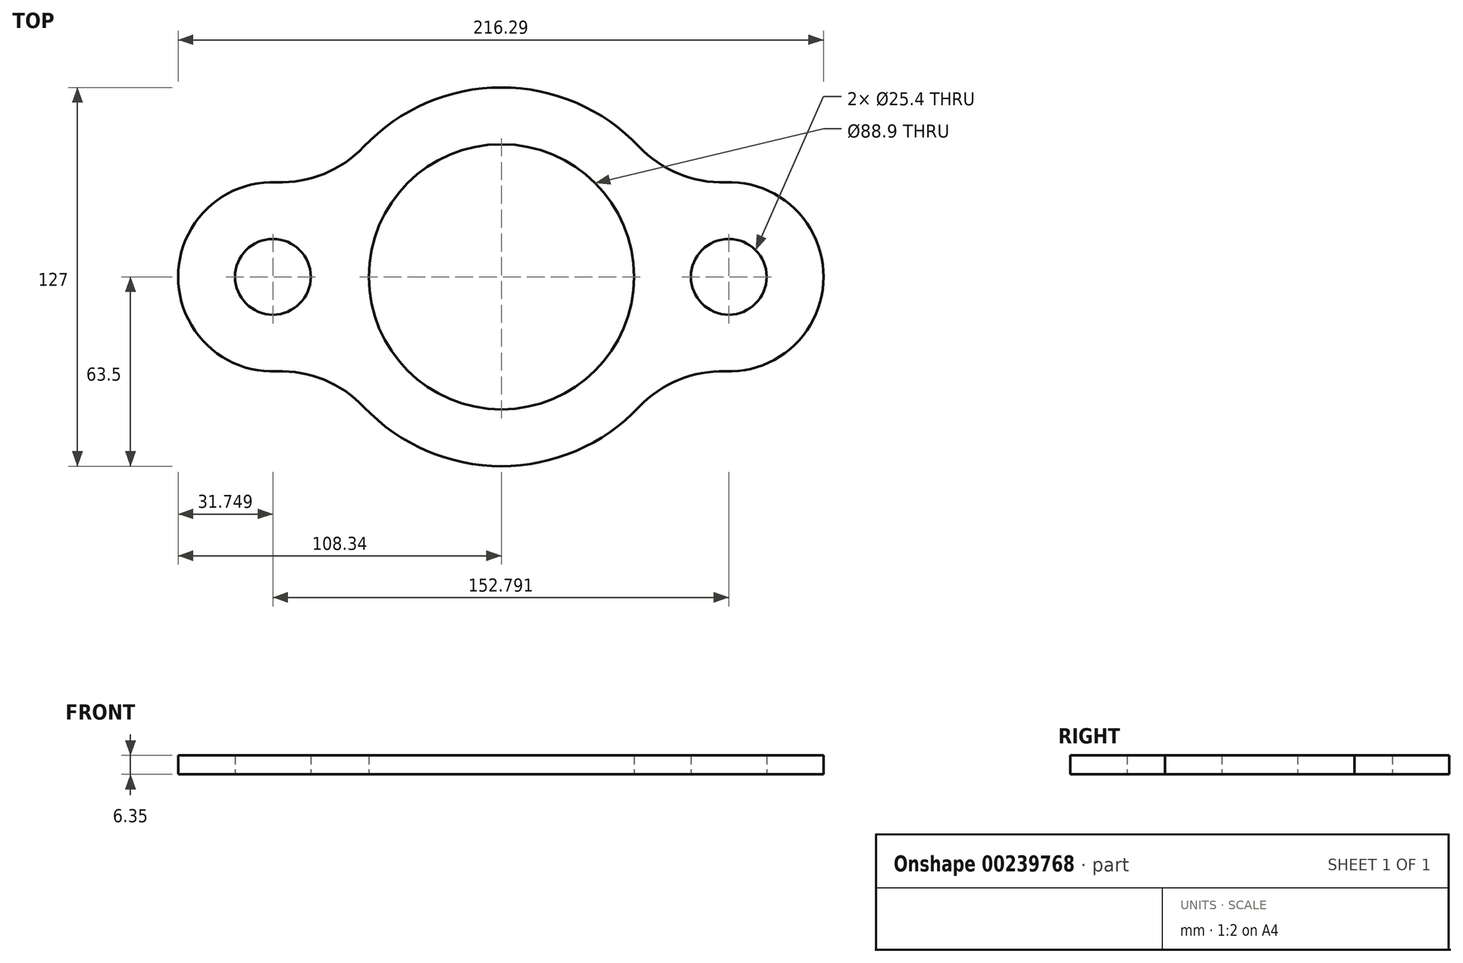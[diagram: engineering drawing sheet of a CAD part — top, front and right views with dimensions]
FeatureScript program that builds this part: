
annotation { "Feature Type Name" : "Feature", "Feature Type Description" : "" }
export const myFeature = defineFeature(function(context is Context, id is Id, definition is map)
    precondition{}
    {
        {
            var Q0;
            Q0=qCreatedBy(makeId("Top.planeOp"),FACE);
            var sketch = newSketch(context, id + "F0", { "sketchPlane" : qUnion([Q0])});
            skCircle(sketch, "E0", {"center": v(0, 0) * mm, "radius": 44.45 * mm});
            skCircle(sketch, "E1", {"center": v(76.2, 0) * mm, "radius": 12.7 * mm});
            skCircle(sketch, "E2", {"center": v(-76.6, 0) * mm, "radius": 12.7 * mm});
            skPoint(sketch, "E3.visualSharp", {"position": v(-56.17, 43.63) * mm});
            skPoint(sketch, "E4.visualSharp", {"position": v(-76.13, 30.64) * mm});
            skCircle(sketch, "E5", {"center": v(0, 0) * mm, "radius": 63.5 * mm});
            skArc(sketch, "E6", {"start": v(-58.04, 25.77) * mm, "mid": v(-108.34, 0) * mm, "end": v(-58.04, -25.77) * mm});
            skArc(sketch, "E7", {"start": v(57.94, -25.98) * mm, "mid": v(107.95, 0) * mm, "end": v(57.94, 25.98) * mm});
            skSolve(sketch);
        }
        {
            var Q0;
            Q0=makeQuery(id+"F0.imprint","IMPRINT",FACE,{"disambiguationData":[TD([[makeQuery(id+"F0.imprint","IMPRINT",EDGE,{"derivedFrom":sQuery(id+"F0.wireOp",EDGE,"E2")}),-1.0]])]});
            var Q1;
            {var subQ0=sQuery(id+"F0.wireOp",EDGE,"E6");var subQ1=sQuery(id+"F0.wireOp",EDGE,"E5");var subQ2=makeQuery(id+"F0.imprint","INTERSECT",VERTEX,{"disambiguationData":[OD(0.0)],"derivedFrom":[subQ1,subQ0]});Q1=makeQuery(id+"F0.imprint","IMPRINT",FACE,{"disambiguationData":[TD([[makeQuery(id+"F0.imprint","IMPRINT",EDGE,{"disambiguationData":[TD([[subQ2,-1.0]])],"derivedFrom":subQ1}),1.0]])]});}
            var Q2;
            {var subQ7=sQuery(id+"F0.wireOp",EDGE,"E0");Q2=makeQuery(id+"F0.imprint","IMPRINT",FACE,{"disambiguationData":[TD([[makeQuery(id+"F0.imprint","IMPRINT",EDGE,{"derivedFrom":subQ7}),-1.0]])]});}
            var Q3;
            {var subQ0=sQuery(id+"F0.wireOp",EDGE,"E5");var subQ1=makeQuery(id+"F0.imprint","INTERSECT",VERTEX,{"derivedFrom":[sQuery(id+"F0.wireOp",EDGE,"E1"),subQ0]});Q3=makeQuery(id+"F0.imprint","IMPRINT",FACE,{"disambiguationData":[TD([[makeQuery(id+"F0.imprint","IMPRINT",EDGE,{"disambiguationData":[TD([[subQ1,-1.0]])],"derivedFrom":subQ0}),1.0]])]});}
            var Q4;
            {var subQ0=sQuery(id+"F0.wireOp",EDGE,"E1");Q4=makeQuery(id+"F0.imprint","IMPRINT",FACE,{"disambiguationData":[TD([[makeQuery(id+"F0.imprint","IMPRINT",EDGE,{"derivedFrom":subQ0}),-1.0]])]});}
            extrude(context, id + "F1", {"entities" : qUnion([Q0, Q1, Q2, Q3, Q4]), "depth" : 6.35 * mm});
        }
        {
            var Q0;
            {var subQ0=sQuery(id+"F0.wireOp",EDGE,"E6");var subQ1=sQuery(id+"F0.wireOp",EDGE,"E5");Q0=makeQuery(id+"F1.opExtrude","SWEPT_EDGE",EDGE,{"disambiguationData":[OSD([subQ1,subQ0]),TDD([makeQuery(id+"F0.imprint","INTERSECT",VERTEX,{"disambiguationData":[OD(1.0)],"derivedFrom":[subQ1,subQ0]})])]});}
            var Q1;
            {var subQ0=sQuery(id+"F0.wireOp",EDGE,"E7");var subQ1=sQuery(id+"F0.wireOp",EDGE,"E5");Q1=makeQuery(id+"F1.opExtrude","SWEPT_EDGE",EDGE,{"disambiguationData":[OSD([subQ1,subQ0]),TDD([makeQuery(id+"F0.imprint","INTERSECT",VERTEX,{"disambiguationData":[OD(1.0)],"derivedFrom":[subQ1,subQ0]})])]});}
            var Q2;
            {var subQ0=sQuery(id+"F0.wireOp",EDGE,"E7");var subQ1=sQuery(id+"F0.wireOp",EDGE,"E5");Q2=makeQuery(id+"F1.opExtrude","SWEPT_EDGE",EDGE,{"disambiguationData":[OSD([subQ1,subQ0]),TDD([makeQuery(id+"F0.imprint","INTERSECT",VERTEX,{"disambiguationData":[OD(0.0)],"derivedFrom":[subQ1,subQ0]})])]});}
            var Q3;
            {var subQ0=sQuery(id+"F0.wireOp",EDGE,"E6");var subQ1=sQuery(id+"F0.wireOp",EDGE,"E5");Q3=makeQuery(id+"F1.opExtrude","SWEPT_EDGE",EDGE,{"disambiguationData":[OSD([subQ1,subQ0]),TDD([makeQuery(id+"F0.imprint","INTERSECT",VERTEX,{"disambiguationData":[OD(0.0)],"derivedFrom":[subQ1,subQ0]})])]});}
            fillet(context, id + "F2", {"entities" : qUnion([Q0, Q1, Q2, Q3]), "radius" : 38.1 * mm, "tangentPropagation" : true, "allowEdgeOverflow" : false});
        }
    });
